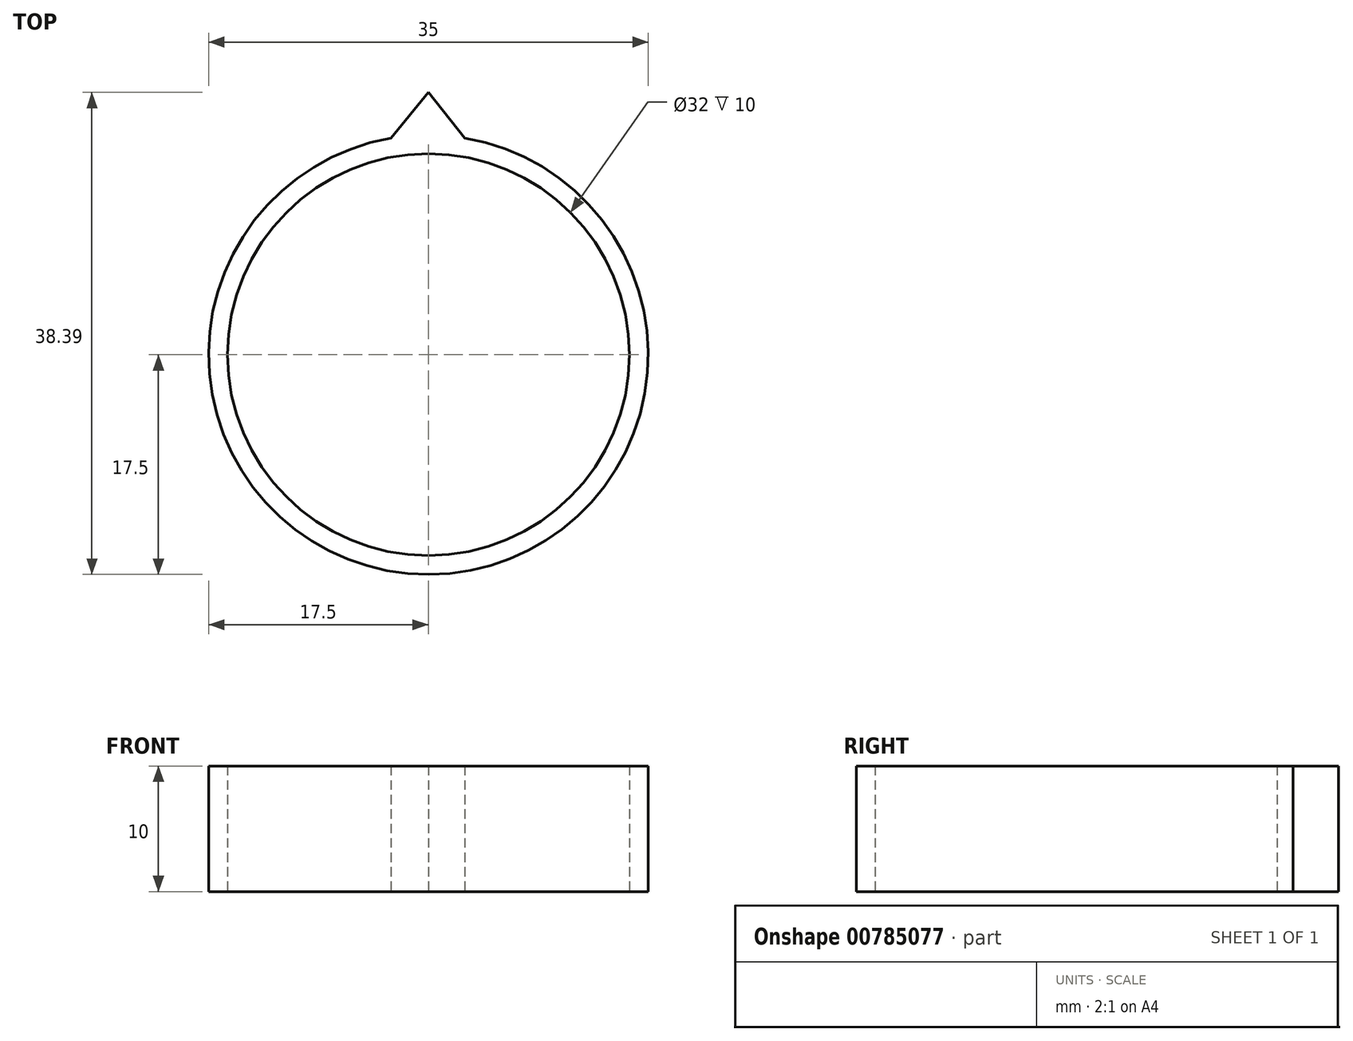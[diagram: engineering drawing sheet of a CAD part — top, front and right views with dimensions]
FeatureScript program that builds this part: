
annotation { "Feature Type Name" : "Feature", "Feature Type Description" : "" }
export const myFeature = defineFeature(function(context is Context, id is Id, definition is map)
    precondition{}
    {
        {
            var Q0;
            Q0=qCreatedBy(makeId("Top.planeOp"),FACE);
            var sketch = newSketch(context, id + "F0", { "sketchPlane" : qUnion([Q0])});
            skCircle(sketch, "E0", {"center": v(0, 0) * mm, "radius": 17.5 * mm});
            skLineSegment(sketch, "E1", {"start": v(-2.97, 17.25) * mm, "end": v(0, 20.9) * mm});
            skLineSegment(sketch, "E2", {"start": v(0, 20.9) * mm, "end": v(2.9, 17.26) * mm});
            skSolve(sketch);
        }
        {
            var Q0;
            Q0 = qSketchRegion(id + "F0", true);
            var Q1;
            Q1 = qBodyType(qCreatedBy(id + "F0" ,EDGE), BodyType.WIRE);
            var Q2;
            Q2=sQuery(id+"F0.wireOp",EDGE,"E0");
            extrude(context, id + "F1", {"entities" : qUnion([Q0]), "surfaceOperationType" : NewSurfaceOperationType.ADD, "surfaceEntities" : qUnion([Q1, Q2]), "depth" : 10 * mm, "offsetDistance" : 25 * mm});
        }
        {
            var Q0;
            Q0=sQuery(id+"F0.wireOp",VERTEX,"E0.center");
            var Q1;
            Q1=makeQuery(id+"F1.opExtrude","SWEPT_BODY",BODY,{"disambiguationData":[OSD([sQuery(id+"F0.wireOp",EDGE,"E0"),sQuery(id+"F0.wireOp",EDGE,"E1"),sQuery(id+"F0.wireOp",EDGE,"E2")])]});
            hole(context, id + "F2", {"style" : HoleStyle.SIMPLE, "endStyle" : HoleEndStyle.THROUGH, "oppositeDirection" : true, "holeDiameter" : 32 * mm, "majorDiameter" : 5 * mm, "isTappedThrough" : true, "tappedDepth" : 12 * mm, "tapClearance" : 3, "locations" : qUnion([Q0]), "scope" : qUnion([Q1])});
        }
    });
